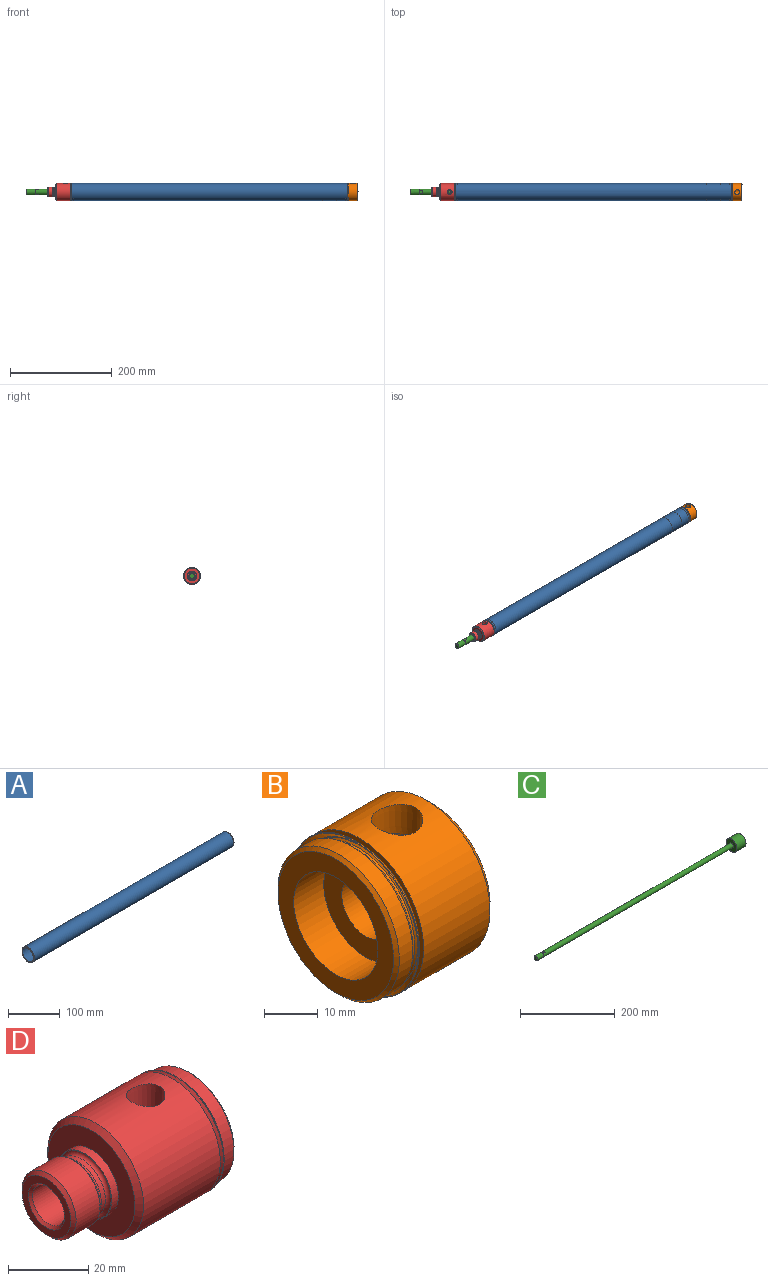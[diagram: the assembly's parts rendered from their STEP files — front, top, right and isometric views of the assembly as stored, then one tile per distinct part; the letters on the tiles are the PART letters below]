
ASSEMBLY  parts=4 mates=3
PART A: 14 faces, bbox 547.5x36.5x36.5 mm
  f0: cone r=16.55mm half-angle=45deg, axis (1,0,0), area 141.2mm2, adj f1,f13
  f1: torus R=15.47mm, axis (1,0,0), area 19.4mm2, adj f0,f2
  f2: cone r=15.38mm half-angle=45deg, axis (-1,0,0), area 50.6mm2, adj f1,f3
  f3: cylinder r=15.01mm len=30.01mm, axis (-1,0,0), area 47.9mm2, adj f2,f4
  f4: cone r=15.01mm half-angle=45deg, axis (1,0,0), area 140.1mm2, adj f3,f5
  f5: cylinder r=16.02mm len=543.67mm, axis (-1,0,0), area 54728mm2, adj f4,f6
  f6: cone r=16.02mm half-angle=45deg, axis (-1,0,0), area 140.1mm2, adj f5,f7
  f7: cylinder r=15.01mm len=30.01mm, axis (-1,0,0), area 47.9mm2, adj f6,f8
  f8: cone r=15.01mm half-angle=45deg, axis (1,0,0), area 50.6mm2, adj f7,f9
  f9: torus R=15.47mm, axis (1,0,0), area 19.4mm2, adj f8,f10
  f10: cone r=15.56mm half-angle=45deg, axis (-1,0,0), area 141.2mm2, adj f9,f11
  f11: torus R=15.83mm, axis (1,0,0), area 84mm2, adj f10,f12
  f12: cylinder r=16.85mm len=544.06mm, axis (-1,0,0), area 57588.3mm2, adj f11,f13
  f13: torus R=15.83mm, axis (1,0,0), area 84mm2, adj f0,f12
PART B: 21 faces, bbox 25.4x33.8x33.8 mm
  f0: cone r=4.62mm half-angle=1.8deg, axis (0,-0.02,1), area 189.7mm2, adj f1,f20
  f1: cylinder r=4.62mm len=9.34mm, axis (0,0.02,-1), area 118.2mm2, adj f0,f3
  f2: cone r=6.35mm half-angle=60deg, axis (-1,0,0), area 136.4mm2, adj f3,f4
  f3: cylinder r=6.35mm len=14.76mm, axis (-1,0,0), area 516.2mm2, adj f1,f2,f9
  f4: plane 30.65x30.65mm, normal (1,0,0), area 729mm2, adj f2,f5
  f5: cone r=16.85mm half-angle=45deg, axis (-1,0,0), area 217.8mm2, adj f4,f20
  f6: plane 33.69x33.69mm, normal (-1,0,0), area 115.9mm2, adj f13,f20
  f7: cylinder r=16.85mm len=33.69mm, axis (-1,0,0), area 21.5mm2, adj f8,f13
  f8: plane 33.69x33.69mm, normal (-1,0,0), area 8.9mm2, adj f7,f10
  f9: plane 22.23x22.23mm, normal (-1,0,0), area 261.3mm2, adj f3,f19
  f10: cone r=16.76mm half-angle=45deg, axis (-1,0,0), area 172.8mm2, adj f8,f11
  f11: torus R=15.47mm, axis (1,0,0), area 19.4mm2, adj f10,f12
  f12: cone r=15.38mm half-angle=45deg, axis (1,0,0), area 50.6mm2, adj f11,f14
  f13: cone r=15.71mm half-angle=45deg, axis (-1,0,0), area 163.9mm2, adj f6,f7
  f14: cylinder r=15.01mm len=30.01mm, axis (-1,0,0), area 47.9mm2, adj f12,f15
  f15: cone r=16.02mm half-angle=45deg, axis (-1,0,0), area 140.1mm2, adj f14,f16
  f16: cylinder r=16.02mm len=32.04mm, axis (-1,0,0), area 358mm2, adj f15,f17
  f17: cone r=15.26mm half-angle=45deg, axis (1,0,0), area 105.9mm2, adj f16,f18
  f18: plane 30.52x30.52mm, normal (-1,0,0), area 343.5mm2, adj f17,f19
  f19: cylinder r=11.11mm len=22.23mm, axis (-1,0,0), area 553.3mm2, adj f9,f18
  f20: cylinder r=16.85mm len=33.69mm, axis (-1,0,0), area 1778.4mm2, adj f0,f5,f6
PART C: 12 faces, bbox 611.2x31.9x31.9 mm
  f0: cylinder r=5.55mm len=565.15mm, axis (-1,0,0), area 19634.6mm2, adj f1,f7,f8,f9,f10,f11
  f1: plane 31.94x31.94mm, normal (-1,0,0), area 704.5mm2, adj f0,f2
  f2: cylinder r=15.97mm len=31.94mm, axis (-1,0,0), area 2706.8mm2, adj f1,f3
  f3: plane 31.94x31.94mm, normal (1,0,0), area 801.3mm2, adj f2
  f4: plane 9.6x9.6mm, normal (-1,0,0), area 72.4mm2, adj f5
  f5: cone r=4.8mm half-angle=45deg, axis (1,0,0), area 34.8mm2, adj f4,f6
  f6: cylinder r=5.56mm len=18.29mm, axis (-1,0,0), area 638.7mm2, adj f5,f7
  f7: plane 11.11x11.11mm, normal (1,0,0), area 5.6mm2, adj f0,f6,f8,f9
  f8: plane 6.35x5.48mm, normal (0,0,-1), area 34.8mm2, adj f0,f7,f11
  f9: plane 6.35x5.48mm, normal (0,0,1), area 34.8mm2, adj f0,f7,f10
  f10: plane 5.48x0.72mm, normal (-1,0,0), area 2.7mm2, adj f0,f9
  f11: plane 5.48x0.72mm, normal (-1,0,0), area 2.7mm2, adj f0,f8
PART D: 29 faces, bbox 50.8x33.8x33.8 mm
  f0: cylinder r=3.17mm len=6.35mm, axis (0,0,-1), area 16.4mm2, adj f1,f10
  f1: cone r=3.17mm half-angle=45deg, axis (0,0,1), area 46.9mm2, adj f0,f2
  f2: cone r=4.54mm half-angle=1.8deg, axis (0,0,1), area 270.1mm2, adj f1,f9
  f3: cone r=16.85mm half-angle=45deg, axis (1,0,0), area 163.9mm2, adj f8,f22
  f4: cone r=15.01mm half-angle=45deg, axis (-1,0,0), area 50.6mm2, adj f5,f23
  f5: torus R=15.47mm, axis (1,0,0), area 19.4mm2, adj f4,f6
  f6: cone r=15.56mm half-angle=45deg, axis (1,0,0), area 172.8mm2, adj f5,f7
  f7: plane 33.69x33.69mm, normal (1,0,0), area 8.9mm2, adj f6,f8
  f8: cylinder r=16.85mm len=33.69mm, axis (-1,0,0), area 21.5mm2, adj f3,f7
  f9: cylinder r=16.85mm len=33.69mm, axis (-1,0,0), area 2780.8mm2, adj f2,f11,f22
  f10: cylinder r=5.61mm len=50.04mm, axis (-1,0,0), area 1731.7mm2, adj f0,f24,f28
  f11: cone r=15.32mm half-angle=45deg, axis (1,0,0), area 217.8mm2, adj f9,f12
  f12: plane 30.65x30.65mm, normal (-1,0,0), area 454.5mm2, adj f11,f13
  f13: cylinder r=9.49mm len=18.99mm, axis (-1,0,0), area 142.4mm2, adj f12,f14
  f14: plane 18.99x18.99mm, normal (-1,0,0), area 10.5mm2, adj f13,f15
  f15: torus R=9.32mm, axis (1,0,0), area 86.9mm2, adj f14,f16
  f16: cylinder r=8.3mm len=16.6mm, axis (-1,0,0), area 74.8mm2, adj f15,f17
  f17: torus R=9.32mm, axis (1,0,0), area 41.9mm2, adj f16,f18
  f18: cone r=9.53mm half-angle=44.8deg, axis (-1,0,0), area 75.3mm2, adj f17,f19
  f19: cylinder r=9.53mm len=19.05mm, axis (-1,0,0), area 503.9mm2, adj f18,f20
  f20: cone r=8.59mm half-angle=45deg, axis (1,0,0), area 75.3mm2, adj f19,f21
  f21: plane 17.18x17.18mm, normal (-1,0,0), area 104.1mm2, adj f20,f28
  f22: plane 33.69x33.69mm, normal (1,0,0), area 115.9mm2, adj f3,f9
  f23: cylinder r=15.01mm len=30.01mm, axis (-1,0,0), area 47.9mm2, adj f4,f27
  f24: plane 30.52x30.52mm, normal (1,0,0), area 632.5mm2, adj f10,f25
  f25: cone r=16.02mm half-angle=45deg, axis (-1,0,0), area 105.9mm2, adj f24,f26
  f26: cylinder r=16.02mm len=32.04mm, axis (-1,0,0), area 364.4mm2, adj f25,f27
  f27: cone r=15.01mm half-angle=45deg, axis (1,0,0), area 140.1mm2, adj f23,f26
  f28: cone r=6.38mm half-angle=45deg, axis (-1,0,0), area 40.6mm2, adj f10,f21
PLACE A t=(45.4,0,0)mm
PLACE B t=(585.77,0,0)mm
PLACE C t=(-17.63,0,0)mm
PLACE D at identity
MATE fastened D.f6 <-> A.f0  axis (1,0,0) through (44.52,0,0)mm
MATE fastened B.f11 <-> A.f0  axis (1,0,0) through (591.99,0,0)mm
MATE slider C.f0 <-> B.f11  axis (1,0,0) through (568.14,0,0)mm
